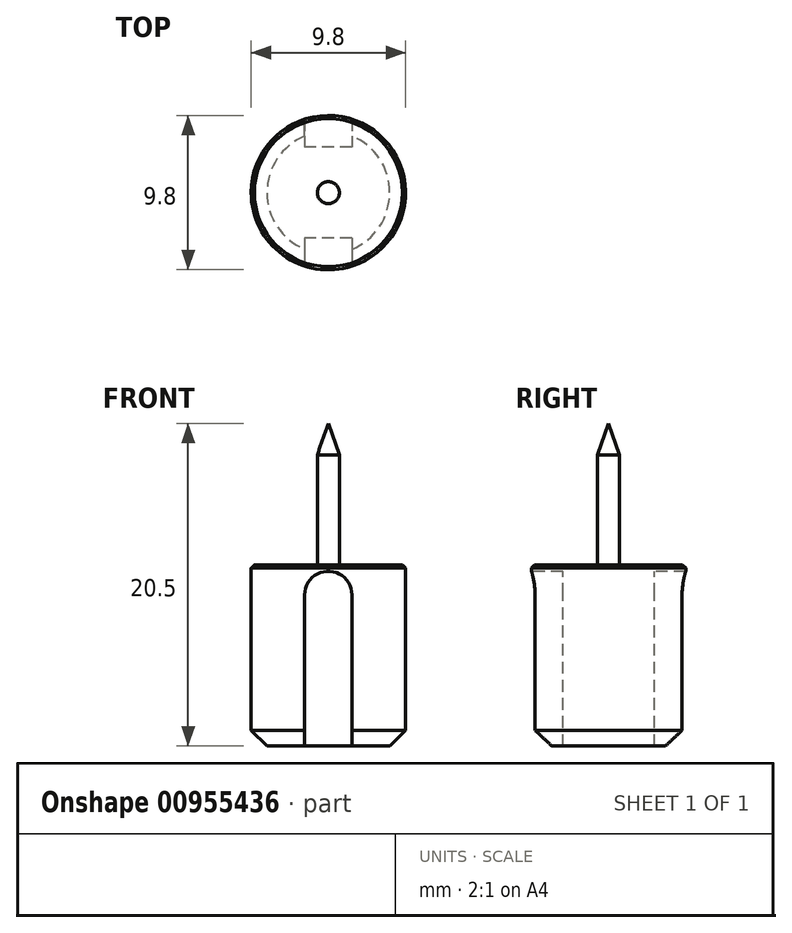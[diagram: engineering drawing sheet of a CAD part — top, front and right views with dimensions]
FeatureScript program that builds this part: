
annotation { "Feature Type Name" : "Feature", "Feature Type Description" : "" }
export const myFeature = defineFeature(function(context is Context, id is Id, definition is map)
    precondition{}
    {
        {
            var Q0;
            Q0=qCreatedBy(makeId("Front.planeOp"),FACE);
            var sketch = newSketch(context, id + "F0", { "sketchPlane" : qUnion([Q0])});
            skLineSegment(sketch, "E0", {"start": v(-4.9, 0) * mm, "end": v(-4.9, 0) * mm});
            skLineSegment(sketch, "E1", {"start": v(-4.9, 0) * mm, "end": v(-4.9, 9) * mm});
            skLineSegment(sketch, "E2", {"start": v(-4.9, 9) * mm, "end": v(-4.9, 9) * mm});
            skLineSegment(sketch, "E3", {"start": v(-4.9, 9) * mm, "end": v(-4.9, 10) * mm});
            skLineSegment(sketch, "E4", {"start": v(-4.9, 10) * mm, "end": v(-0.7, 10) * mm});
            skLineSegment(sketch, "E5", {"start": v(-0.7, 10) * mm, "end": v(-0.7, 19) * mm});
            skLineSegment(sketch, "E6", {"start": v(-0.7, 19) * mm, "end": v(0, 19) * mm});
            skLineSegment(sketch, "E7", {"start": v(0, 19) * mm, "end": v(0, 0) * mm});
            skLineSegment(sketch, "E8", {"start": v(0, 0) * mm, "end": v(-4.9, 0) * mm});
            skSolve(sketch);
        }
        {
            var Q0;
            Q0 = qSketchRegion(id + "F0", true);
            var Q1;
            Q1=sQuery(id+"F0.wireOp",EDGE,"E7");
            revolve(context, id + "F1", {"surfaceOperationType" : NewSurfaceOperationType.NEW, "entities" : qUnion([Q0]), "axis" : qUnion([Q1]), "revolveType" : RevolveType.FULL});
        }
        {
            var Q0;
            Q0=qCreatedBy(makeId("Front.planeOp"),FACE);
            var sketch = newSketch(context, id + "F2", { "sketchPlane" : qUnion([Q0])});
            skLineSegment(sketch, "E9.left", {"start": v(1.5, 8.1) * mm, "end": v(1.5, 0) * mm});
            skLineSegment(sketch, "E9.right", {"start": v(-1.5, 8.1) * mm, "end": v(-1.5, 0) * mm});
            skArc(sketch, "E10", {"start": v(1.5, 8.1) * mm, "mid": v(0, 9.6) * mm, "end": v(-1.5, 8.1) * mm});
            skPoint(sketch, "E11.orphan", {"position": v(-1.5, 11.9) * mm});
            skPoint(sketch, "E12.orphan", {"position": v(1.5, 11.84) * mm});
            skLineSegment(sketch, "E13", {"start": v(-1.5, 0) * mm, "end": v(1.5, 0) * mm});
            skSolve(sketch);
        }
        {
            var Q0;
            Q0 = qSketchRegion(id + "F2", true);
            extrude(context, id + "F3", {"entities" : qUnion([Q0]), "operationType" : NewBodyOperationType.REMOVE, "oppositeDirection" : true, "depth" : 25 * mm, "offsetDistance" : 25 * mm, "hasSecondDirection" : true, "secondDirectionOppositeDirection" : true, "secondDirectionDepth" : 2 * mm});
        }
        {
            var Q0;
            Q0 = qSketchRegion(id + "F2", true);
            extrude(context, id + "F4", {"entities" : qUnion([Q0]), "operationType" : NewBodyOperationType.REMOVE, "oppositeDirection" : true, "depth" : 25 * mm, "offsetDistance" : 25 * mm});
        }
        {
            var Q0;
            Q0=makeQuery(id+"F1.opRevolve","SWEPT_FACE",FACE,{"disambiguationData":[OSD([sQuery(id+"F0.wireOp",EDGE,"E8")])]});
            extrude(context, id + "F5", {"entities" : qUnion([Q0]), "operationType" : NewBodyOperationType.ADD, "depth" : 1.5 * mm, "offsetDistance" : 25 * mm});
        }
        {
            var Q0;
            Q0=makeQuery(id+"F5.opExtrude","CAP_EDGE",EDGE,{"disambiguationData":[OSD([sQuery(id+"F0.wireOp",EDGE,"E1"),sQuery(id+"F0.wireOp",EDGE,"E8")])],"isStart":false});
            chamfer(context, id + "F6", {"entities" : qUnion([Q0]), "width" : 1 * mm, "tangentPropagation" : true});
        }
        {
            var Q0;
            Q0=makeQuery(id+"F1.opRevolve","SWEPT_EDGE",EDGE,{"disambiguationData":[OSD([sQuery(id+"F0.wireOp",EDGE,"E5"),sQuery(id+"F0.wireOp",EDGE,"E6")])]});
            chamfer(context, id + "F7", {"entities" : qUnion([Q0]), "chamferType" : ChamferType.TWO_OFFSETS, "width1" : 0.7 * mm, "oppositeDirection" : false, "width2" : 2 * mm, "tangentPropagation" : true});
        }
        {
            var Q0;
            Q0=makeQuery(id+"F1.opRevolve","SWEPT_EDGE",EDGE,{"disambiguationData":[OSD([sQuery(id+"F0.wireOp",EDGE,"E3"),sQuery(id+"F0.wireOp",EDGE,"E4")])]});
            chamfer(context, id + "F8", {"entities" : qUnion([Q0]), "width" : 0.2 * mm, "tangentPropagation" : true});
        }
        {
            var Q0;
            {var subQ0=sQuery(id+"F2.wireOp",EDGE,"E13");Q0=makeQuery(id+"F5.boolean.opBoolean","MERGE",FACE,{"derivedFrom":[makeQuery(id+"F4.boolean.opBoolean","COPY",FACE,{"derivedFrom":makeQuery(id+"F4.opExtrude","CAP_FACE",FACE,{"disambiguationData":[OSD([sQuery(id+"F2.wireOp",EDGE,"E9.left"),sQuery(id+"F2.wireOp",EDGE,"E9.right"),sQuery(id+"F2.wireOp",EDGE,"E10"),subQ0])],"isStart":true})}),makeQuery(id+"F5.opExtrude","SWEPT_FACE",FACE,{"disambiguationData":[OSD([subQ0])]})]});}
            extrude(context, id + "F9", {"entities" : qUnion([Q0]), "operationType" : NewBodyOperationType.REMOVE, "oppositeDirection" : true, "depth" : 25 * mm, "offsetDistance" : 25 * mm});
        }
        {
            var Q0;
            {var subQ0=sQuery(id+"F2.wireOp",EDGE,"E9.right");var subQ2=sQuery(id+"F0.wireOp",EDGE,"E8");Q0=makeQuery(id+"F9.boolean.opBoolean","SPLIT",FACE,{"disambiguationData":[TD([makeQuery(id+"F3.boolean.opBoolean","COPY",FACE,{"derivedFrom":makeQuery(id+"F3.opExtrude","SWEPT_FACE",FACE,{"disambiguationData":[OSD([subQ0])]})})])],"derivedFrom":makeQuery(id+"F5.opExtrude","CAP_FACE",FACE,{"disambiguationData":[OSD([subQ2])],"isStart":false})});}
            var sketch = newSketch(context, id + "F10", { "sketchPlane" : qUnion([Q0])});
            skLineSegment(sketch, "E14.bottom", {"start": v(2.25, 2.9) * mm, "end": v(-2.25, 2.9) * mm});
            skLineSegment(sketch, "E14.top", {"start": v(2.25, -2.9) * mm, "end": v(-2.25, -2.9) * mm});
            skLineSegment(sketch, "E14.left", {"start": v(2.25, 2.9) * mm, "end": v(2.25, -2.9) * mm});
            skLineSegment(sketch, "E14.right", {"start": v(-2.25, 2.9) * mm, "end": v(-2.25, -2.9) * mm});
            skPoint(sketch, "E14.middle", {"position": v(0, 0) * mm});
            skSolve(sketch);
        }
        {
            var Q0;
            Q0 = qSketchRegion(id + "F10", true);
            var Q1;
            Q1=makeQuery(id+"F1.opRevolve","SWEPT_BODY",BODY,{"disambiguationData":[OSD([sQuery(id+"F0.wireOp",EDGE,"E1"),sQuery(id+"F0.wireOp",EDGE,"E3"),sQuery(id+"F0.wireOp",EDGE,"E4"),sQuery(id+"F0.wireOp",EDGE,"E5"),sQuery(id+"F0.wireOp",EDGE,"E6"),sQuery(id+"F0.wireOp",EDGE,"E7"),sQuery(id+"F0.wireOp",EDGE,"E8")])]});
            extrude(context, id + "F11", {"entities" : qUnion([Q0]), "operationType" : NewBodyOperationType.ADD, "endBound" : BoundingType.UP_TO_BODY, "oppositeDirection" : true, "depth" : 25 * mm, "endBoundEntityBody" : qUnion([Q1]), "offsetDistance" : 25 * mm});
        }
    });
